# Revit family: Clevertronics_EPIC-1500-SEN-EM_AUB03510220001
name_source: partatom
category: Lighting Fixtures
units: mm (PartAtom-declared; Revit-internal decimal feet)

## family parameters
Cut with Voids When Loaded = No
Host = Face
Light Source = Yes
Part Type = Normal
Room Calculation Point = No
Round Connector Dimension = Use Diameter
Shared = No

## types (1)
- EPIC-1500-SEN-EM_AUB03510220001
    Apparent Load = 0 VA
    Clevertronics_AS2293 Classification = C0=D40 C90=D25
    Clevertronics_Annotation Size = 0 mm  [stored 0 ft]
    Clevertronics_Applicable Standards = AS/NZS3820, CISPR15, AS/NZS2293.3
    Clevertronics_Battery = 3.2V 3000mAh
    Clevertronics_Battery Type = Lithium Iron Phosphate
    Clevertronics_Charger Method = Intelligent current limited constant voltage
    Clevertronics_Construction = Powder Coated Sheet Metal Base, Co-extruded IP40 PC Diffuser Assembly, PC End Caps
    Clevertronics_Diffuser = Co-extruded IP40 PC Diffuser Assembly
    Clevertronics_Dimensions Main Enclosure = L 1533mm x W 72mm x H 78mm
    Clevertronics_Driver/ Ballast = LC 57W, 700-1050mA, flexC Ip SNC4
    Clevertronics_Earth Leakage = 0.152mA
    Clevertronics_Emergency Driver = LED Driver : 1330069 EM Driver: AUM03670010001
    Clevertronics_Height = 78 mm  [stored 0.255906 ft]
    Clevertronics_IP Rating = IP20
    Clevertronics_Impact Rating = IK03
    Clevertronics_Inrush Current = 28.4A, <88µs
    Clevertronics_Length = 1533 mm  [stored 5.02953 ft]
    Clevertronics_MIC Number = AUB03510220001
    Clevertronics_Material = Clevertronics_Plycarbonate Base
    Clevertronics_Mounting = Surface Mount
    Clevertronics_Operating Mode = SUSTAINED
    Clevertronics_Operating Temperature = 1°C to 40°C
    Clevertronics_Operating Voltage = 220-240V~ 50Hz
    Clevertronics_Power Consumption = 47.58W
    Clevertronics_Power Factor = 0.90 @ High Output
    Clevertronics_Product Description = Epic 1500mm Diffused Emergency Batten, Switchable Colour & Output
    Clevertronics_Replacement Battery = Battery: 1560150
    Clevertronics_Supply Current = 180mA +/- 20mA
    Clevertronics_Total Lumen Output = 6117 lm (128.6 lm/W)
    Clevertronics_Weight = 2.2 Kg
    Clevertronics_Width = 72 mm  [stored 0.23622 ft]
    Color Filter = 16777215
    Default Elevation = 1200 mm
    Description = Epic 1500mm Diffused Emergency Batten, Switchable Colour
    Dimming Lamp Color Temperature Shift = <None>
    Emit from Line Length = 610 mm
    Lamp = Dual LED strip module, 3000K warm white, 5700K cool white, >50,000hr life, Ra>80__L70/B50 Ta 40°C; Reported >54,000hr, Projected 158,000hr__L80/B50 Ta 40°C; Reported >54,000hr, Projected 99,000hr
    Manufacturer = Clevertronics
    Model = EPIC-1500-SEN-EM
    Photometric Web File = EPIC-1500-4K_IESA_G_TUV7191314725_20230817.IES
    Tilt Angle = -90.00°

note: [stored X ft] marks values corroborated as IEEE doubles in the binary element streams (Revit-internal decimal feet)

## geometry (parser evidence)
native form markers: Blend x2, Sweep x3
no freeform markers — native parametric forms only
